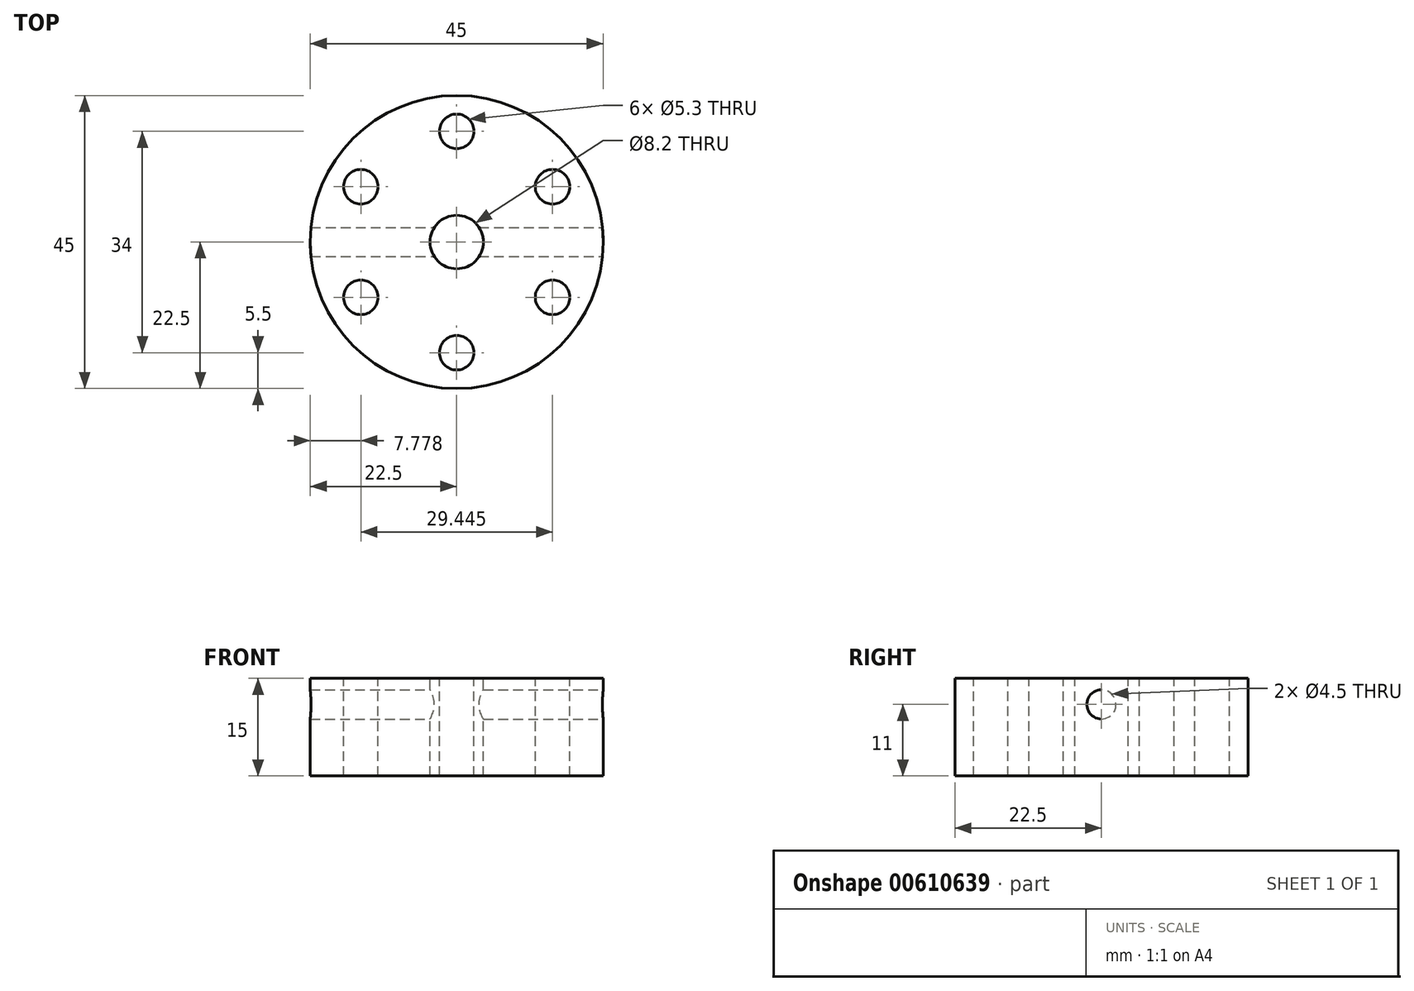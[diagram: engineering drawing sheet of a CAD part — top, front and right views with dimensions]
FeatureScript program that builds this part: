
annotation { "Feature Type Name" : "Feature", "Feature Type Description" : "" }
export const myFeature = defineFeature(function(context is Context, id is Id, definition is map)
    precondition{}
    {
        {
            var Q0;
            Q0=qCreatedBy(makeId("Top.planeOp"),FACE);
            var sketch = newSketch(context, id + "F0", { "sketchPlane" : qUnion([Q0])});
            skCircle(sketch, "E0", {"center": v(0, 0) * mm, "radius": 22.5 * mm});
            skSolve(sketch);
        }
        {
            var Q0;
            Q0=makeQuery(id+"F0.imprint","IMPRINT",FACE,{"disambiguationData":[TD([[makeQuery(id+"F0.imprint","IMPRINT",EDGE,{"derivedFrom":sQuery(id+"F0.wireOp",EDGE,"E0")}),1.0]])]});
            extrude(context, id + "F1", {"entities" : qUnion([Q0]), "depth" : 15 * mm, "offsetDistance" : 25 * mm});
        }
        {
            var Q0;
            Q0=makeQuery(id+"F1.opExtrude","CAP_FACE",FACE,{"disambiguationData":[OSD([sQuery(id+"F0.wireOp",EDGE,"E0")])],"isStart":false});
            var sketch = newSketch(context, id + "F2", { "sketchPlane" : qUnion([Q0])});
            skPoint(sketch, "E1", {"position": v(0, 0) * mm});
            skSolve(sketch);
        }
        {
            var Q0;
            Q0=sQuery(id+"F2.wireOp",VERTEX,"E1");
            var Q1;
            Q1=makeQuery(id+"F1.opExtrude","SWEPT_BODY",BODY,{"disambiguationData":[OSD([sQuery(id+"F0.wireOp",EDGE,"E0")])]});
            hole(context, id + "F3", {"style" : HoleStyle.SIMPLE, "endStyle" : HoleEndStyle.THROUGH, "holeDiameter" : 8.2 * mm, "majorDiameter" : 5 * mm, "tappedDepth" : 12 * mm, "tapClearance" : 3, "locations" : qUnion([Q0]), "scope" : qUnion([Q1])});
        }
        {
            var Q0;
            Q0=makeQuery(id+"F1.opExtrude","CAP_FACE",FACE,{"disambiguationData":[OSD([sQuery(id+"F0.wireOp",EDGE,"E0")])],"isStart":false});
            var sketch = newSketch(context, id + "F4", { "sketchPlane" : qUnion([Q0])});
            skPoint(sketch, "E2", {"position": v(0, 17) * mm});
            skPoint(sketch, "E3.1.0", {"position": v(-14.72, 8.5) * mm});
            skPoint(sketch, "E3.2.0", {"position": v(-14.72, -8.5) * mm});
            skPoint(sketch, "E3.3.0", {"position": v(0, -17) * mm});
            skPoint(sketch, "E3.4.0", {"position": v(14.72, -8.5) * mm});
            skPoint(sketch, "E3.5.0", {"position": v(14.72, 8.5) * mm});
            skPoint(sketch, "E3.center", {"position": v(0, 0) * mm});
            skSolve(sketch);
        }
        {
            var Q0;
            Q0=sQuery(id+"F4.wireOp",VERTEX,"E2");
            var Q1;
            Q1=sQuery(id+"F4.wireOp",VERTEX,"E3.5.0");
            var Q2;
            Q2=sQuery(id+"F4.wireOp",VERTEX,"E3.4.0");
            var Q3;
            Q3=sQuery(id+"F4.wireOp",VERTEX,"E3.3.0");
            var Q4;
            Q4=sQuery(id+"F4.wireOp",VERTEX,"E3.2.0");
            var Q5;
            Q5=sQuery(id+"F4.wireOp",VERTEX,"E3.1.0");
            var Q6;
            Q6=makeQuery(id+"F1.opExtrude","SWEPT_BODY",BODY,{"disambiguationData":[OSD([sQuery(id+"F0.wireOp",EDGE,"E0")])]});
            hole(context, id + "F5", {"style" : HoleStyle.SIMPLE, "endStyle" : HoleEndStyle.THROUGH, "holeDiameter" : 5.3 * mm, "majorDiameter" : 5 * mm, "tappedDepth" : 12 * mm, "tapClearance" : 3, "locations" : qUnion([Q0, Q1, Q2, Q3, Q4, Q5]), "scope" : qUnion([Q6])});
        }
        {
            var Q0;
            Q0=qCreatedBy(makeId("Right.planeOp"),FACE);
            var sketch = newSketch(context, id + "F6", { "sketchPlane" : qUnion([Q0])});
            skCircle(sketch, "E4", {"center": v(0, 11) * mm, "radius": 2.25 * mm});
            skSolve(sketch);
        }
        {
            var Q0;
            Q0=qSketchRegion(id+"F6",true);
            extrude(context, id + "F7", {"entities" : qUnion([Q0]), "operationType" : NewBodyOperationType.REMOVE, "endBound" : BoundingType.SYMMETRIC, "oppositeDirection" : true, "depth" : 100 * mm, "offsetDistance" : 25 * mm});
        }
    });
